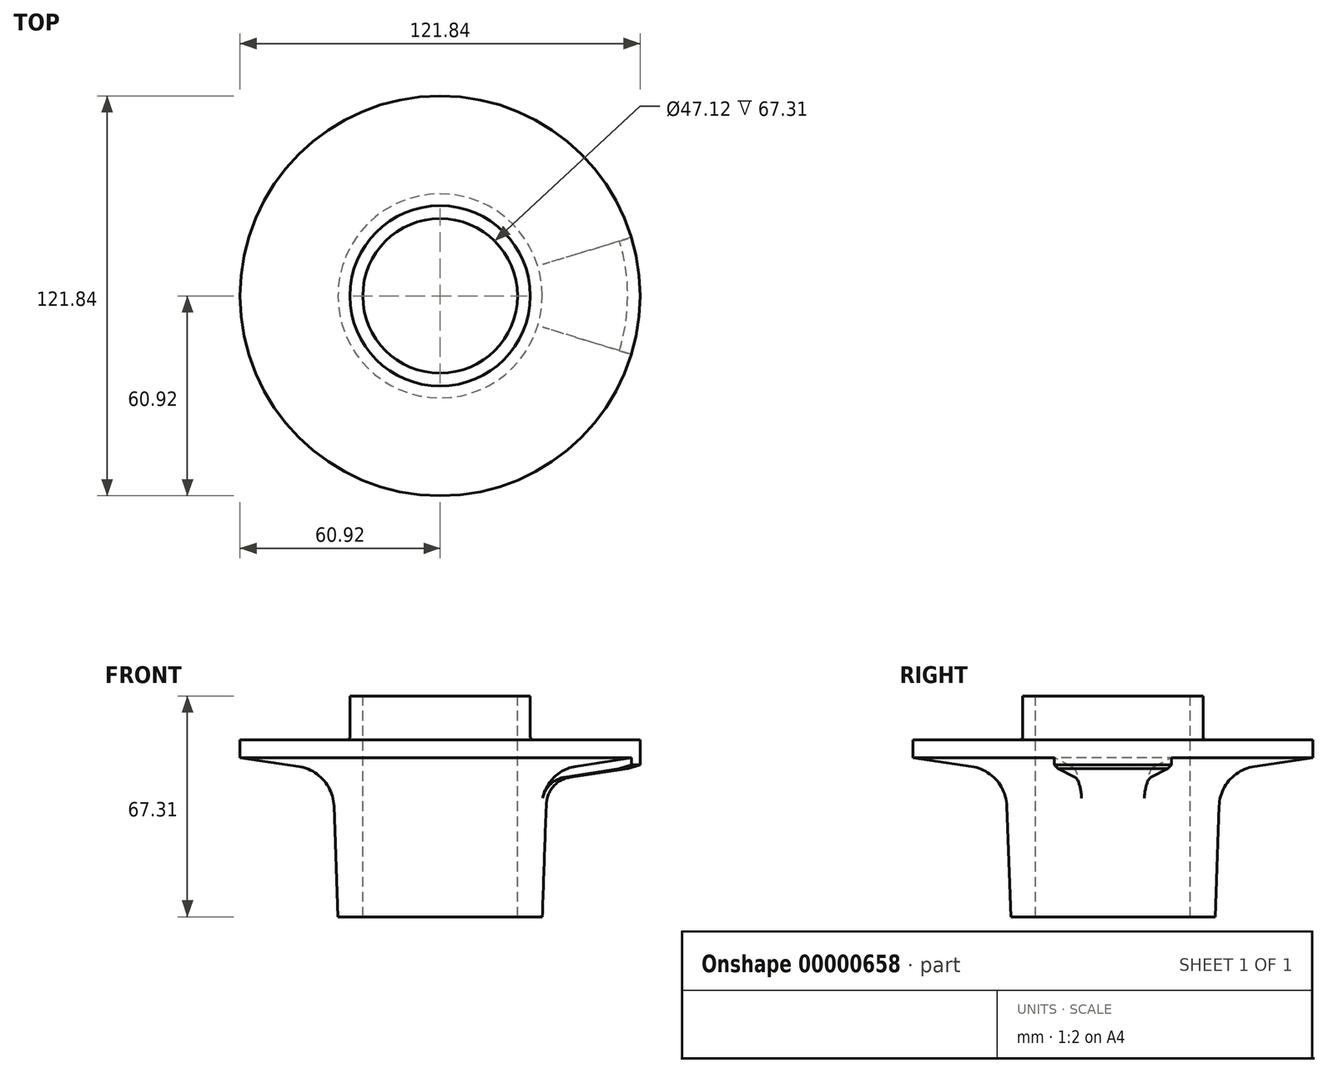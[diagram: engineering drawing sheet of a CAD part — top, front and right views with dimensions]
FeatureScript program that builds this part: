
annotation { "Feature Type Name" : "Feature", "Feature Type Description" : "" }
export const myFeature = defineFeature(function(context is Context, id is Id, definition is map)
    precondition{}
    {
        {
            var Q0;
            Q0 = qCreatedBy(makeId("Front.planeOp"), FACE);
            var sketch = newSketch(context, id + "F0", { "sketchPlane" : qUnion([Q0])});
            skLineSegment(sketch, "E0", {"start": v(0, 0) * mm, "end": v(0, -67.31) * mm, "construction": true});
            skLineSegment(sketch, "E1", {"start": v(23.56, 0) * mm, "end": v(23.56, -67.31) * mm});
            skLineSegment(sketch, "E2", {"start": v(23.56, -67.31) * mm, "end": v(31.12, -67.31) * mm});
            skLineSegment(sketch, "E3", {"start": v(31.12, -67.31) * mm, "end": v(32.32, -33.6) * mm});
            skArc(sketch, "E4", {"start": v(43.11, -21.49) * mm, "mid": v(35.53, -25.6) * mm, "end": v(32.32, -33.6) * mm});
            skLineSegment(sketch, "E5", {"start": v(43.11, -21.49) * mm, "end": v(60.92, -18.8) * mm});
            skLineSegment(sketch, "E6", {"start": v(60.92, -18.8) * mm, "end": v(60.92, -13.34) * mm});
            skLineSegment(sketch, "E7", {"start": v(60.92, -13.34) * mm, "end": v(28.24, -13.34) * mm});
            skArc(sketch, "E8", {"start": v(27.48, -12.57) * mm, "mid": v(27.7, -13.11) * mm, "end": v(28.24, -13.34) * mm});
            skLineSegment(sketch, "E9", {"start": v(27.48, -12.57) * mm, "end": v(27.48, 0) * mm});
            skLineSegment(sketch, "E10", {"start": v(27.48, 0) * mm, "end": v(23.56, 0) * mm});
            skLineSegment(sketch, "E11.0.MirrorCS", {"start": v(-27.48, 0) * mm, "end": v(-23.56, 0) * mm, "construction": true});
            skArc(sketch, "E11.1.MirrorCS", {"start": v(-43.11, -21.49) * mm, "mid": v(-35.53, -25.6) * mm, "end": v(-32.32, -33.6) * mm, "construction": true});
            skLineSegment(sketch, "E11.2.MirrorCS", {"start": v(-27.48, -12.57) * mm, "end": v(-27.48, 0) * mm, "construction": true});
            skLineSegment(sketch, "E11.4.MirrorCS", {"start": v(-60.92, -13.33) * mm, "end": v(-28.24, -13.33) * mm, "construction": true});
            skLineSegment(sketch, "E11.6.MirrorCS", {"start": v(-27.48, 0) * mm, "end": v(-27.48, 0) * mm});
            skLineSegment(sketch, "E11.7.MirrorCS", {"start": v(-60.92, -18.8) * mm, "end": v(-60.92, -13.34) * mm, "construction": true});
            skLineSegment(sketch, "E11.8.MirrorCS", {"start": v(-27.48, 0) * mm, "end": v(-27.48, 0) * mm});
            skLineSegment(sketch, "E11.11.MirrorCS", {"start": v(-23.56, -67.31) * mm, "end": v(-31.11, -67.31) * mm, "construction": true});
            skLineSegment(sketch, "E11.19.MirrorCS", {"start": v(-43.11, -21.49) * mm, "end": v(-60.92, -18.8) * mm, "construction": true});
            skLineSegment(sketch, "E11.20.MirrorCS", {"start": v(-23.56, 0) * mm, "end": v(-23.56, -67.31) * mm, "construction": true});
            skLineSegment(sketch, "E11.25.MirrorCS", {"start": v(-31.12, -67.31) * mm, "end": v(-32.32, -33.6) * mm, "construction": true});
            skArc(sketch, "E11.27.MirrorCS", {"start": v(-27.48, -12.57) * mm, "mid": v(-27.7, -13.11) * mm, "end": v(-28.24, -13.33) * mm, "construction": true});
            skSolve(sketch);
        }
        {
            var Q0;
            Q0=makeQuery(id+"F0.imprint","IMPRINT",FACE,{"disambiguationData":[TD([[makeQuery(id+"F0.imprint","IMPRINT",EDGE,{"derivedFrom":sQuery(id+"F0.wireOp",EDGE,"E1")}),1.0]])]});
            var Q1;
            Q1=sQuery(id+"F0.wireOp",EDGE,"E0");
            revolve(context, id + "F1", {"entities" : qUnion([Q0]), "axis" : qUnion([Q1]), "revolveType" : RevolveType.FULL});
        }
        {
            var Q0;
            Q0 = qCreatedBy(makeId("Front.planeOp"), FACE);
            var sketch = newSketch(context, id + "F2", { "sketchPlane" : qUnion([Q0])});
            skLineSegment(sketch, "E12.0", {"start": v(43.11, -21.49) * mm, "end": v(60.92, -18.8) * mm});
            skArc(sketch, "E12.1", {"start": v(43.11, -21.49) * mm, "mid": v(36.41, -24.7) * mm, "end": v(32.66, -31.12) * mm});
            skLineSegment(sketch, "E13", {"start": v(60.92, -18.8) * mm, "end": v(60.92, -20.96) * mm});
            skLineSegment(sketch, "E14", {"start": v(60.92, -20.96) * mm, "end": v(57.11, -22.17) * mm});
            skLineSegment(sketch, "E15", {"start": v(57.11, -22.17) * mm, "end": v(39.48, -24.83) * mm});
            skLineSegment(sketch, "E16", {"start": v(57.11, -22.17) * mm, "end": v(60.92, -21.6) * mm, "construction": true});
            skLineSegment(sketch, "E17", {"start": v(60.92, -21.6) * mm, "end": v(60.92, -20.96) * mm, "construction": true});
            skArc(sketch, "E18", {"start": v(39.48, -24.83) * mm, "mid": v(35.1, -26.93) * mm, "end": v(32.66, -31.12) * mm});
            skPoint(sketch, "E19.orphan", {"position": v(32.32, -33.6) * mm});
            skSolve(sketch);
        }
        {
            var Q0;
            Q0=makeQuery(id+"F2.imprint","IMPRINT",FACE,{"disambiguationData":[TD([[makeQuery(id+"F2.imprint","IMPRINT",EDGE,{"derivedFrom":sQuery(id+"F2.wireOp",EDGE,"E12.0")}),-1.0]])]});
            var Q1;
            Q1=sQuery(id+"F0.wireOp",EDGE,"E0");
            revolve(context, id + "F3", {"operationType" : NewBodyOperationType.ADD, "entities" : qUnion([Q0]), "axis" : qUnion([Q1]), "revolveType" : RevolveType.TWO_DIRECTIONS, "angle" : 17 * degree, "angleBack" : 343 * degree});
        }
        {
            var Q0;
            Q0=makeQuery(id+"F1.opRevolve","SWEPT_FACE",FACE,{"disambiguationData":[OSD([sQuery(id+"F0.wireOp",EDGE,"E7")])]});
            var sketch = newSketch(context, id + "F4", { "sketchPlane" : qUnion([Q0])});
            skCircle(sketch, "E20", {"center": v(50, 0) * mm, "radius": 6.3 * mm});
            skSolve(sketch);
        }
        {
            var Q0;
            Q0=makeQuery(id+"F1.opRevolve","SWEPT_FACE",FACE,{"disambiguationData":[OSD([sQuery(id+"F0.wireOp",EDGE,"E7")])]});
            cPlane(context, id + "F5", {"entities" : qUnion([Q0]), "cplaneType" : CPlaneType.OFFSET, "offset" : 7.92 * mm, "oppositeDirection" : true, "width" : 152.4 * mm, "height" : 152.4 * mm});
        }
    });
